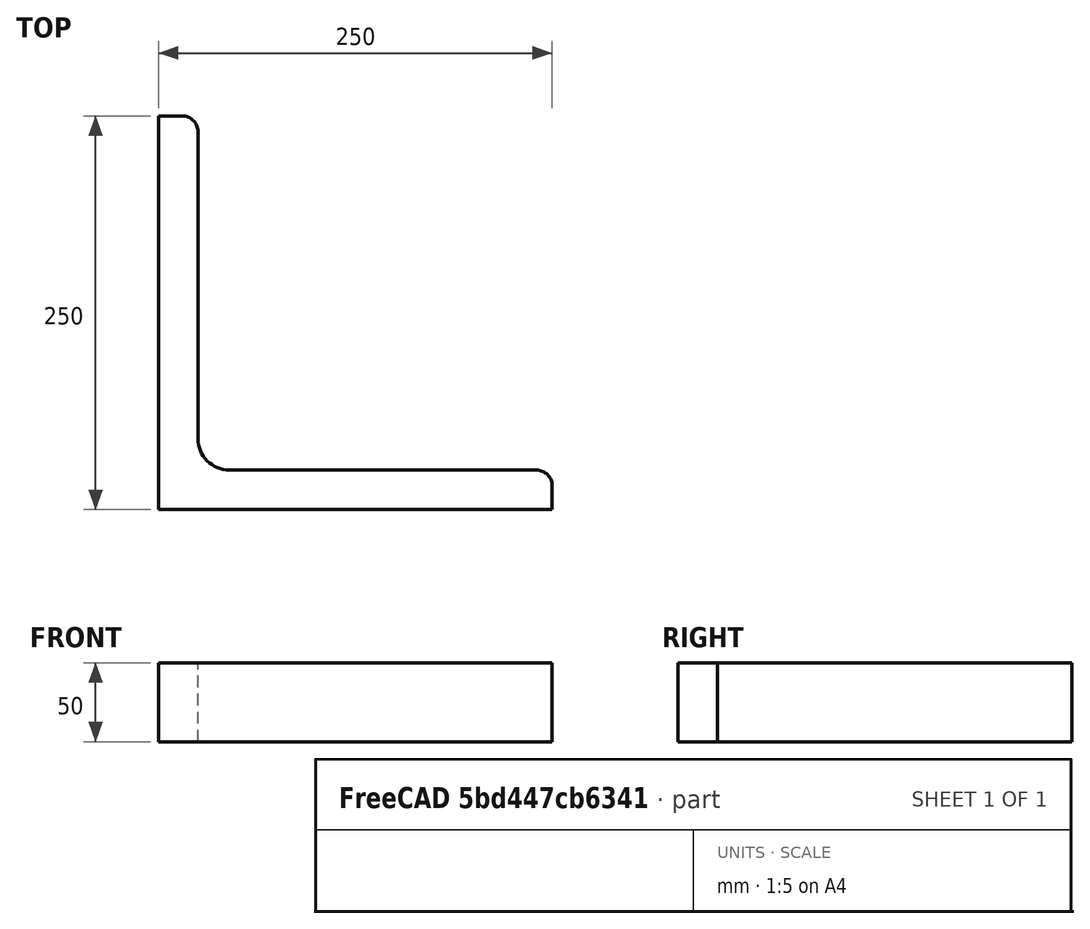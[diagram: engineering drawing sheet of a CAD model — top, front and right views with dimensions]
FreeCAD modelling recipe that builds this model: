
FCSTD DOCUMENT  (FreeCAD 0.15R4671 (Git))
Label: Angle Bar L250x250x25 EN10056 S235JR
License: All rights reserved
LicenseURL: http://en.wikipedia.org/wiki/All_rights_reserved
objects: Sketcher::SketchObject×1, Part::Extrusion×1
note: 2 computed .brp shape members not serialized (recipe doc carries the construction recipe); baked Part::Feature solids carry a one-line shape summary decoded from their .brp

FEATURE [Sketcher::SketchObject] Sketch
  sketch-geometry (9):
    g0: LineSegment StartX=0 StartY=0 StartZ=0 EndX=250 EndY=0 EndZ=0
    g1: LineSegment StartX=250 StartY=0 StartZ=0 EndX=250 EndY=15 EndZ=0
    g2: LineSegment StartX=240 StartY=25 StartZ=0 EndX=45 EndY=25 EndZ=0
    g3: LineSegment StartX=0 StartY=0 StartZ=0 EndX=0 EndY=250 EndZ=0
    g4: LineSegment StartX=0 StartY=250 StartZ=0 EndX=15 EndY=250 EndZ=0
    g5: LineSegment StartX=25 StartY=240 StartZ=0 EndX=25 EndY=45 EndZ=0
    g6: ArcOfCircle CenterX=45 CenterY=45 CenterZ=0 NormalX=0 NormalY=0 NormalZ=1 Radius=20 StartAngle=3.14159 EndAngle=4.71239
    g7: ArcOfCircle CenterX=15 CenterY=240 CenterZ=0 NormalX=0 NormalY=0 NormalZ=1 Radius=10 StartAngle=0 EndAngle=1.5708
    g8: ArcOfCircle CenterX=240 CenterY=15 CenterZ=0 NormalX=0 NormalY=0 NormalZ=1 Radius=10 StartAngle=0 EndAngle=1.5708
  constraints (23):
    c: Coincident(g0,g-1)
    c: Horizontal(g0)
    c: Coincident(g1,g0)
    c: Vertical(g1)
    c: Horizontal(g2)
    c: Coincident(g3,g-1)
    c: Vertical(g3)
    c: Coincident(g4,g3)
    c: Horizontal(g4)
    c: Vertical(g5)
    c: Tangent(g5,g6) = -1.5708
    c: Tangent(g2,g6) = 1.5708
    c: Tangent(g4,g7) = 1.5708
    c: Tangent(g5,g7) = 1.5708
    c: Tangent(g2,g8) = -1.5708
    c: Tangent(g1,g8) = -1.5708
    c: DistanceX(g0) = 250
    c: DistanceY(g3) = 250
    c: DistanceY(g0,g2) = 25
    c: DistanceX(g3,g5) = 25
    c: Radius(g6) = 20
    c: Radius(g8) = 10
    c: Radius(g7) = 10
FEATURE [Part::Extrusion] Extrude  label="Angle Bar L250x250x25 EN10056 S235JR"
  Base = -> Sketch
  Dir = (0,0,50)
  Solid = true
